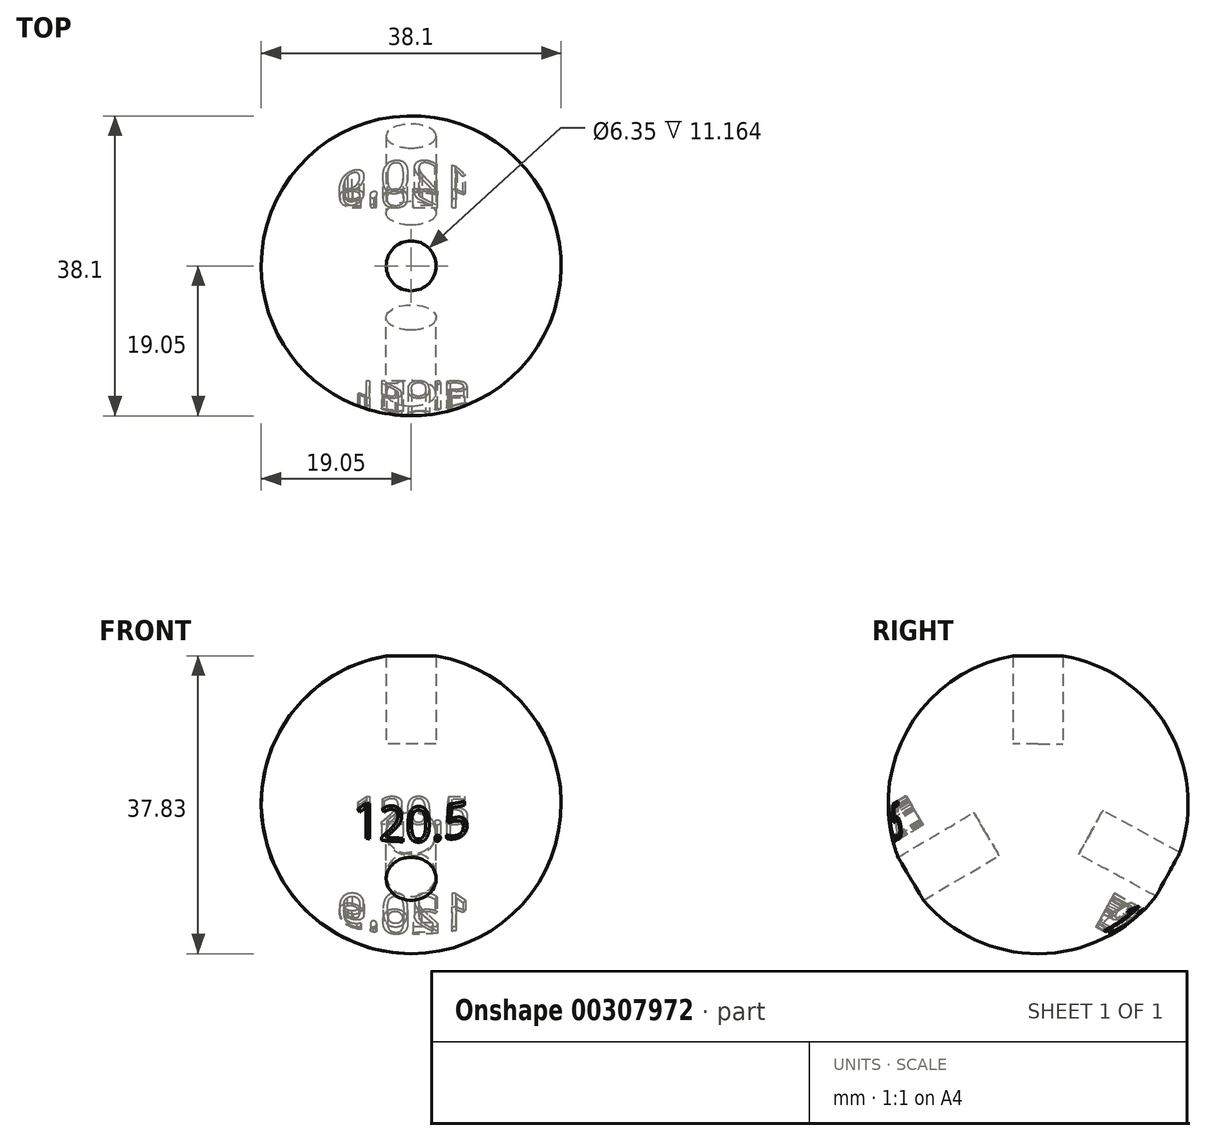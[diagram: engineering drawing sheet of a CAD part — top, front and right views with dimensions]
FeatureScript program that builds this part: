
annotation { "Feature Type Name" : "Feature", "Feature Type Description" : "" }
export const myFeature = defineFeature(function(context is Context, id is Id, definition is map)
    precondition{}
    {
        {
            var Q0;
            Q0=qCreatedBy(makeId("Front.planeOp"),FACE);
            var sketch = newSketch(context, id + "F0", { "sketchPlane" : qUnion([Q0])});
            skArc(sketch, "E0", {"start": v(0, 19.05) * mm, "mid": v(-19.05, 0) * mm, "end": v(0, -19.05) * mm});
            skLineSegment(sketch, "E1", {"start": v(0, 19.05) * mm, "end": v(0, -19.05) * mm});
            skSolve(sketch);
        }
        {
            var Q0;
            Q0=qCreatedBy(makeId("Top.planeOp"),FACE);
            var sketch = newSketch(context, id + "F1", { "sketchPlane" : qUnion([Q0])});
            skCircle(sketch, "E2", {"center": v(0, 0) * mm, "radius": 19.05 * mm});
            skSolve(sketch);
        }
        {
            var Q0;
            Q0=makeQuery(id+"F0.imprint","IMPRINT",FACE,{"disambiguationData":[TD([[makeQuery(id+"F0.imprint","IMPRINT",EDGE,{"derivedFrom":sQuery(id+"F0.wireOp",EDGE,"E0")}),1.0]])]});
            var Q1;
            Q1=sQuery(id+"F1.wireOp",EDGE,"E2");
            revolve(context, id + "F2", {"entities" : qUnion([Q0]), "axis" : qUnion([Q1]), "revolveType" : RevolveType.FULL});
        }
        {
            var Q0;
            Q0=qCreatedBy(makeId("Front.planeOp"),FACE);
            var sketch = newSketch(context, id + "F3", { "sketchPlane" : qUnion([Q0])});
            skLineSegment(sketch, "E3", {"start": v(0, 0) * mm, "end": v(76.32, 0) * mm, "construction": true});
            skLineSegment(sketch, "E4", {"start": v(0, 0) * mm, "end": v(0, 76.7) * mm, "construction": true});
            skSolve(sketch);
        }
        {
            var Q0;
            Q0=qCreatedBy(makeId("Top.planeOp"),FACE);
            cPlane(context, id + "F4", {"entities" : qUnion([Q0]), "cplaneType" : CPlaneType.OFFSET, "offset" : 7.62 * mm, "width" : 152.4 * mm, "height" : 152.4 * mm});
        }
        {
            var Q0;
            Q0=qCreatedBy(id+"F4.planeOp",FACE);
            var sketch = newSketch(context, id + "F5", { "sketchPlane" : qUnion([Q0])});
            skCircle(sketch, "E5", {"center": v(0, 0) * mm, "radius": 3.17 * mm});
            skSolve(sketch);
        }
        {
            var Q0;
            Q0 = qSketchRegion(id + "F5", true);
            extrude(context, id + "F6", {"entities" : qUnion([Q0]), "depth" : 76.2 * mm});
        }
        {
            var Q0;
            Q0=makeQuery(id+"F6.opExtrude","SWEPT_BODY",BODY,{"disambiguationData":[OSD([sQuery(id+"F5.wireOp",EDGE,"E5")])]});
            var Q1;
            Q1=sQuery(id+"F3.wireOp",EDGE,"E3");
            transform(context, id + "F7", {"entities" : qUnion([Q0]), "transformType" : TransformType.ROTATION, "transformAxis" : qUnion([Q1]), "angle" : 120.5 * degree, "makeCopy" : true});
        }
        {
            var Q0;
            Q0=makeQuery(id+"F7.opPattern","COPY",BODY,{"derivedFrom":makeQuery(id+"F6.opExtrude","SWEPT_BODY",BODY,{"disambiguationData":[OSD([sQuery(id+"F5.wireOp",EDGE,"E5")])]}),"instanceName":"1"});
            var Q1;
            Q1=sQuery(id+"F3.wireOp",EDGE,"E3");
            transform(context, id + "F8", {"entities" : qUnion([Q0]), "transformType" : TransformType.ROTATION, "transformAxis" : qUnion([Q1]), "angle" : 120.9 * degree, "makeCopy" : true});
        }
        {
            var Q0;
            Q0=makeQuery(id+"F7.opPattern","COPY",FACE,{"derivedFrom":makeQuery(id+"F6.opExtrude","CAP_FACE",FACE,{"disambiguationData":[OSD([sQuery(id+"F5.wireOp",EDGE,"E5")])],"isStart":false}),"instanceName":"1"});
            cPlane(context, id + "F9", {"entities" : qUnion([Q0]), "cplaneType" : CPlaneType.OFFSET, "offset" : 63.5 * mm, "oppositeDirection" : true, "width" : 152.4 * mm, "height" : 152.4 * mm});
        }
        {
            var Q0;
            Q0=qCreatedBy(id+"F9.planeOp",FACE);
            var sketch = newSketch(context, id + "F10", { "sketchPlane" : qUnion([Q0])});
            skText(sketch, "E6", { "text": "120.5", "fontName": "OpenSans-Regular.ttf"});
            const initialGuessF10  = {"E6": [-0.00732, 0.00517, 1, 0, 0.00416]};
            skSetInitialGuess(sketch, initialGuessF10);
            skSolve(sketch);
        }
        {
            var Q0;
            Q0 = qSketchRegion(id + "F10", true);
            extrude(context, id + "F11", {"entities" : qUnion([Q0]), "operationType" : NewBodyOperationType.REMOVE, "oppositeDirection" : true, "depth" : 6.35 * mm});
        }
        {
            var Q0;
            Q0=makeQuery(id+"F8.opPattern","COPY",FACE,{"derivedFrom":makeQuery(id+"F7.opPattern","COPY",FACE,{"derivedFrom":makeQuery(id+"F6.opExtrude","CAP_FACE",FACE,{"disambiguationData":[OSD([sQuery(id+"F5.wireOp",EDGE,"E5")])],"isStart":false}),"instanceName":"1"}),"instanceName":"1"});
            cPlane(context, id + "F12", {"entities" : qUnion([Q0]), "cplaneType" : CPlaneType.OFFSET, "offset" : 63.5 * mm, "oppositeDirection" : true, "width" : 152.4 * mm, "height" : 152.4 * mm});
        }
        {
            var Q0;
            Q0=qCreatedBy(id+"F12.planeOp",FACE);
            var sketch = newSketch(context, id + "F13", { "sketchPlane" : qUnion([Q0])});
            skText(sketch, "E7", { "text": "120.9", "fontName": "OpenSans-Regular.ttf"});
            const initialGuessF13  = {"E7": [-0.00748, -0.01013, 1, 0, 0.00478]};
            skSetInitialGuess(sketch, initialGuessF13);
            skSolve(sketch);
        }
        {
            var Q0;
            Q0 = qSketchRegion(id + "F13", true);
            extrude(context, id + "F14", {"entities" : qUnion([Q0]), "operationType" : NewBodyOperationType.REMOVE, "oppositeDirection" : true, "depth" : 6.35 * mm});
        }
        {
            var Q0;
            Q0=makeQuery(id+"F6.opExtrude","SWEPT_BODY",BODY,{"disambiguationData":[OSD([sQuery(id+"F5.wireOp",EDGE,"E5")])]});
            var Q1;
            Q1=makeQuery(id+"F7.opPattern","COPY",BODY,{"derivedFrom":makeQuery(id+"F6.opExtrude","SWEPT_BODY",BODY,{"disambiguationData":[OSD([sQuery(id+"F5.wireOp",EDGE,"E5")])]}),"instanceName":"1"});
            var Q2;
            Q2=makeQuery(id+"F8.opPattern","COPY",BODY,{"derivedFrom":makeQuery(id+"F7.opPattern","COPY",BODY,{"derivedFrom":makeQuery(id+"F6.opExtrude","SWEPT_BODY",BODY,{"disambiguationData":[OSD([sQuery(id+"F5.wireOp",EDGE,"E5")])]}),"instanceName":"1"}),"instanceName":"1"});
            var Q3;
            Q3=makeQuery(id+"F2.opRevolve","SWEPT_BODY",BODY,{"disambiguationData":[OSD([sQuery(id+"F0.wireOp",EDGE,"E0"),sQuery(id+"F0.wireOp",EDGE,"E1")])]});
            booleanBodies(context, id + "F15", {"operationType" : BooleanOperationType.SUBTRACTION, "tools" : qUnion([Q0, Q1, Q2]), "targets" : qUnion([Q3])});
        }
    });
